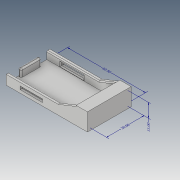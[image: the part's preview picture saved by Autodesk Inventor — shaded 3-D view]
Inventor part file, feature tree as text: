
AUTODESK INVENTOR PART (.ipt)
format: ipt  version: 2019 (Build 230136000, 136)  size: 209,920 bytes
history: native  units: mm
features: sketch x7, extrude x7, other x4, fillet x2, projected_geometry x1
ambient origin geometry x8: Origin, YZ Plane, XZ Plane, XY Plane, X Axis, Y Axis, Z Axis, Center Point
bodies: Solid1 (feature_tree)
feature tree (21):
  other  "Annotations"
  sketch  "Sketch1"  dims[d0=57.0mm d1=27.0mm]
  extrude  "Extrusion1"  Depth=27.0mm
  extrude  "Extrusion2"  Depth=1.5mm TaperAngle=0.0deg
  sketch  "Sketch4"  dims[d7=7.0mm d8=6.0mm d9=0.0mm]
  extrude  "Extrusion3"  Depth=2.5mm
  extrude  "Extrusion4"  Depth=6.0mm TaperAngle=0.0deg
  extrude  "Extrusion5"  Depth=1.5mm
  extrude  "Extrusion6"  Depth=4.5mm TaperAngle=0.0deg
  extrude  "Extrusion7"  Depth=30.0mm TaperAngle=0.0deg
  fillet  "Fillet1"  Radius=1.5mm
  fillet  "Fillet2"  Radius=9.0mm
  sketch  "Sketch2"  dims[d2=4.0mm d3=1.5mm d4=0.0mm]
  sketch  "Sketch3"  dims[d5=2.5mm d6=7.0mm]
  projected_geometry  "Projected Loop1"
  sketch  "Sketch5"  dims[d10=5.0mm d11=1.5mm]
  sketch  "Sketch6"  dims[d12=7.0mm d13=4.5mm d14=0.0mm]
  sketch  "Sketch7"  dims[d15=4.5mm d16=0.0mm d17=4.5mm d18=0.0mm d19=1.5mm d20=0.0mm d21=9.0mm d22=18.0mm d23=2.5mm d24=1.5mm d25=0.0mm d35=2.5mm d36=2.5mm d37=1.0mm d38=0.8mm d26=0.0mm d27=10.0mm d28=11.0mm d29=0.0mm d30=10.0mm d31=62.5mm d32=0.0mm d33=10.0mm d34=30.0mm]
  other  "Linear Dimension 1"
  other  "Linear Dimension 2"
  other  "Linear Dimension 3"
